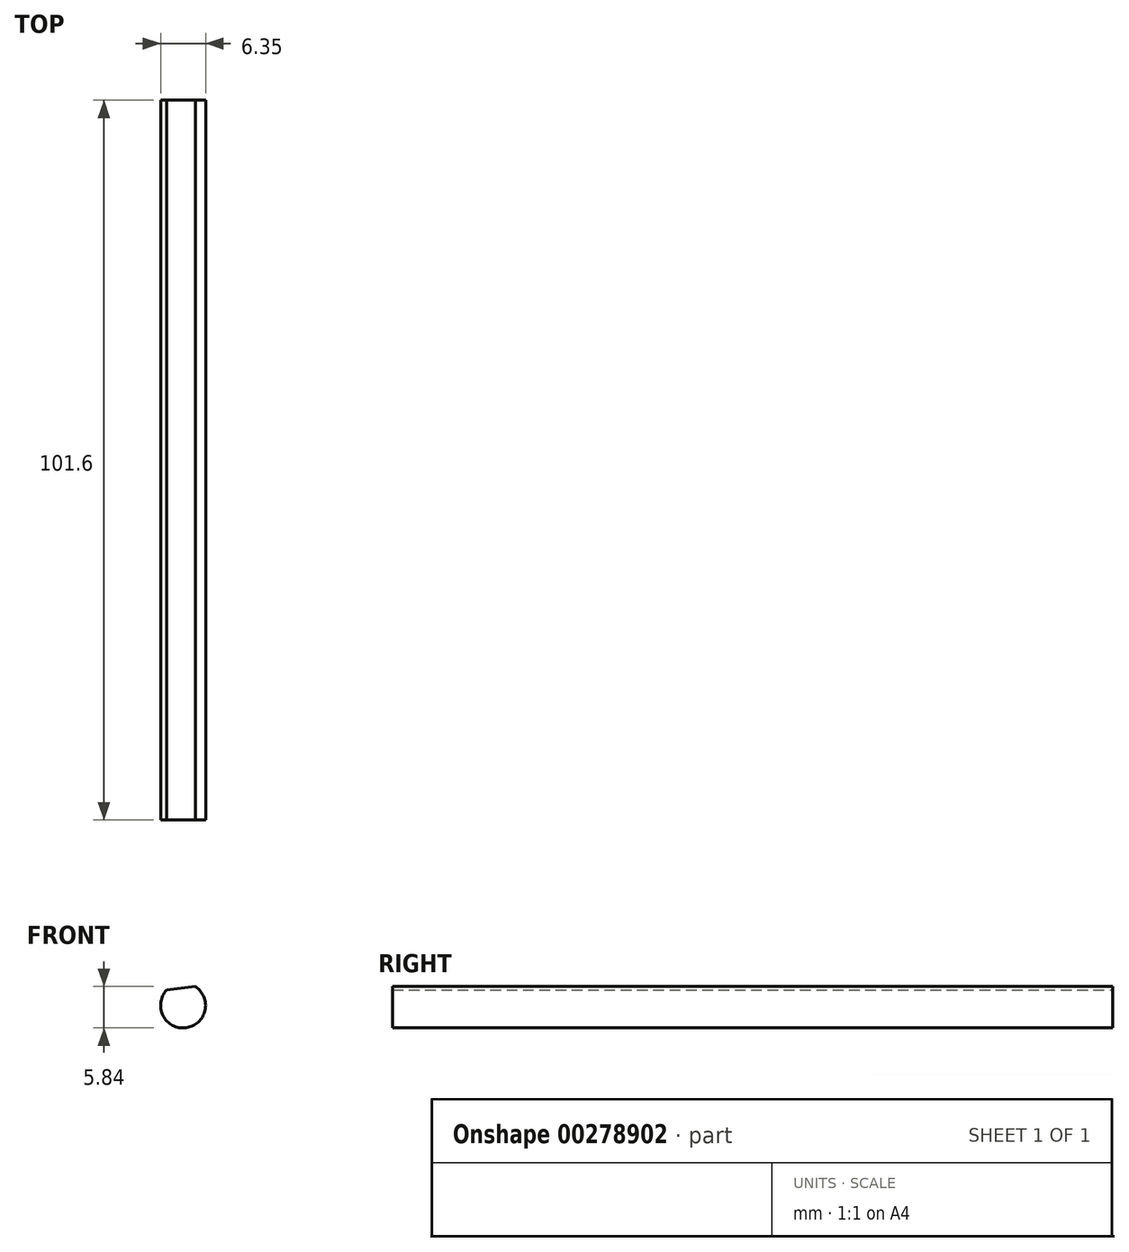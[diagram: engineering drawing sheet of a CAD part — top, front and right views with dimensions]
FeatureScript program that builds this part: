
annotation { "Feature Type Name" : "Feature", "Feature Type Description" : "" }
export const myFeature = defineFeature(function(context is Context, id is Id, definition is map)
    precondition{}
    {
        {
            var Q0;
            Q0=qCreatedBy(makeId("Front.planeOp"),FACE);
            var sketch = newSketch(context, id + "F0", { "sketchPlane" : qUnion([Q0])});
            skLineSegment(sketch, "E0", {"start": v(-107, 40.23) * mm, "end": v(-102.96, 40.73) * mm});
            skArc(sketch, "E1", {"start": v(-107, 40.23) * mm, "mid": v(-104.28, 34.91) * mm, "end": v(-102.96, 40.73) * mm});
            skSolve(sketch);
        }
        {
            var Q0;
            Q0 = qSketchRegion(id + "F0", true);
            extrude(context, id + "F1", {"entities" : qUnion([Q0]), "depth" : 101.6 * mm});
        }
    });
